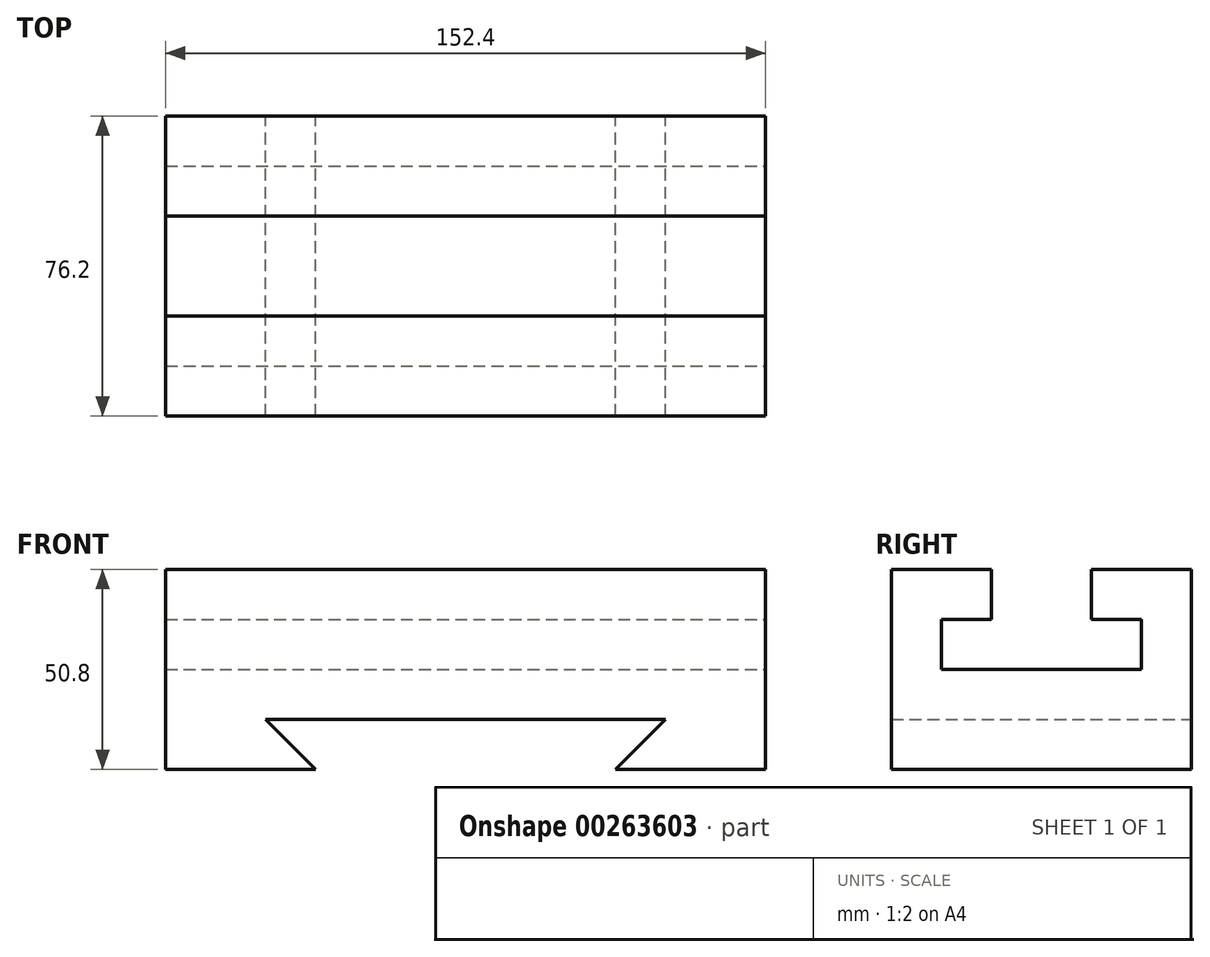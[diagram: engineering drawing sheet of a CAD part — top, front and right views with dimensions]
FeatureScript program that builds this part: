
annotation { "Feature Type Name" : "Feature", "Feature Type Description" : "" }
export const myFeature = defineFeature(function(context is Context, id is Id, definition is map)
    precondition{}
    {
        {
            var Q0;
            Q0=qCreatedBy(makeId("Front.planeOp"),FACE);
            var sketch = newSketch(context, id + "F0", { "sketchPlane" : qUnion([Q0])});
            skLineSegment(sketch, "E0.top", {"start": v(-75.98, 50.8) * mm, "end": v(76.42, 50.8) * mm});
            skLineSegment(sketch, "E0.left", {"start": v(-75.98, 0) * mm, "end": v(-75.98, 50.8) * mm});
            skLineSegment(sketch, "E0.right", {"start": v(76.42, 0) * mm, "end": v(76.42, 50.8) * mm});
            skLineSegment(sketch, "E1", {"start": v(-75.98, 0) * mm, "end": v(-37.88, 0) * mm});
            skLineSegment(sketch, "E2", {"start": v(76.42, 0) * mm, "end": v(38.32, 0) * mm});
            skLineSegment(sketch, "E3", {"start": v(-50.58, 12.7) * mm, "end": v(51.02, 12.7) * mm});
            skLineSegment(sketch, "E4", {"start": v(-50.58, 12.7) * mm, "end": v(-37.88, 0) * mm});
            skLineSegment(sketch, "E5", {"start": v(38.32, 0) * mm, "end": v(51.02, 12.7) * mm});
            skSolve(sketch);
        }
        {
            var Q0;
            Q0=makeQuery(id+"F0.imprint","IMPRINT",FACE,{"disambiguationData":[TD([[makeQuery(id+"F0.imprint","IMPRINT",EDGE,{"derivedFrom":sQuery(id+"F0.wireOp",EDGE,"E0.top")}),-1.0]])]});
            extrude(context, id + "F1", {"entities" : qUnion([Q0]), "depth" : 76.2 * mm});
        }
        {
            var Q0;
            Q0=makeQuery(id+"F1.opExtrude","SWEPT_FACE",FACE,{"disambiguationData":[OSD([sQuery(id+"F0.wireOp",EDGE,"E0.right")])]});
            var sketch = newSketch(context, id + "F2", { "sketchPlane" : qUnion([Q0])});
            skLineSegment(sketch, "E6", {"start": v(-76.2, 50.8) * mm, "end": v(-50.8, 50.8) * mm});
            skLineSegment(sketch, "E7", {"start": v(0, 50.8) * mm, "end": v(-25.4, 50.8) * mm});
            skLineSegment(sketch, "E8", {"start": v(-50.8, 50.8) * mm, "end": v(-50.8, 38.1) * mm});
            skLineSegment(sketch, "E9", {"start": v(-25.4, 50.8) * mm, "end": v(-25.4, 38.1) * mm});
            skLineSegment(sketch, "E10", {"start": v(-50.8, 38.1) * mm, "end": v(-63.5, 38.1) * mm});
            skLineSegment(sketch, "E11", {"start": v(-25.4, 38.1) * mm, "end": v(-12.7, 38.1) * mm});
            skLineSegment(sketch, "E12", {"start": v(-12.7, 38.1) * mm, "end": v(-12.7, 25.4) * mm});
            skLineSegment(sketch, "E13", {"start": v(-12.7, 25.4) * mm, "end": v(-63.5, 25.4) * mm});
            skPoint(sketch, "E13.endSnap0", {"position": v(-76.2, 25.4) * mm});
            skLineSegment(sketch, "E14", {"start": v(-63.5, 25.4) * mm, "end": v(-63.5, 38.1) * mm});
            skSolve(sketch);
        }
        {
            var Q0;
            {var subQ1=sQuery(id+"F2.wireOp",EDGE,"E8");Q0=makeQuery(id+"F2.imprint","IMPRINT",FACE,{"disambiguationData":[TD([[makeQuery(id+"F2.imprint","IMPRINT",EDGE,{"derivedFrom":subQ1}),1.0]])]});}
            extrude(context, id + "F3", {"entities" : qUnion([Q0]), "operationType" : NewBodyOperationType.REMOVE, "oppositeDirection" : true, "depth" : 152.4 * mm});
        }
    });
